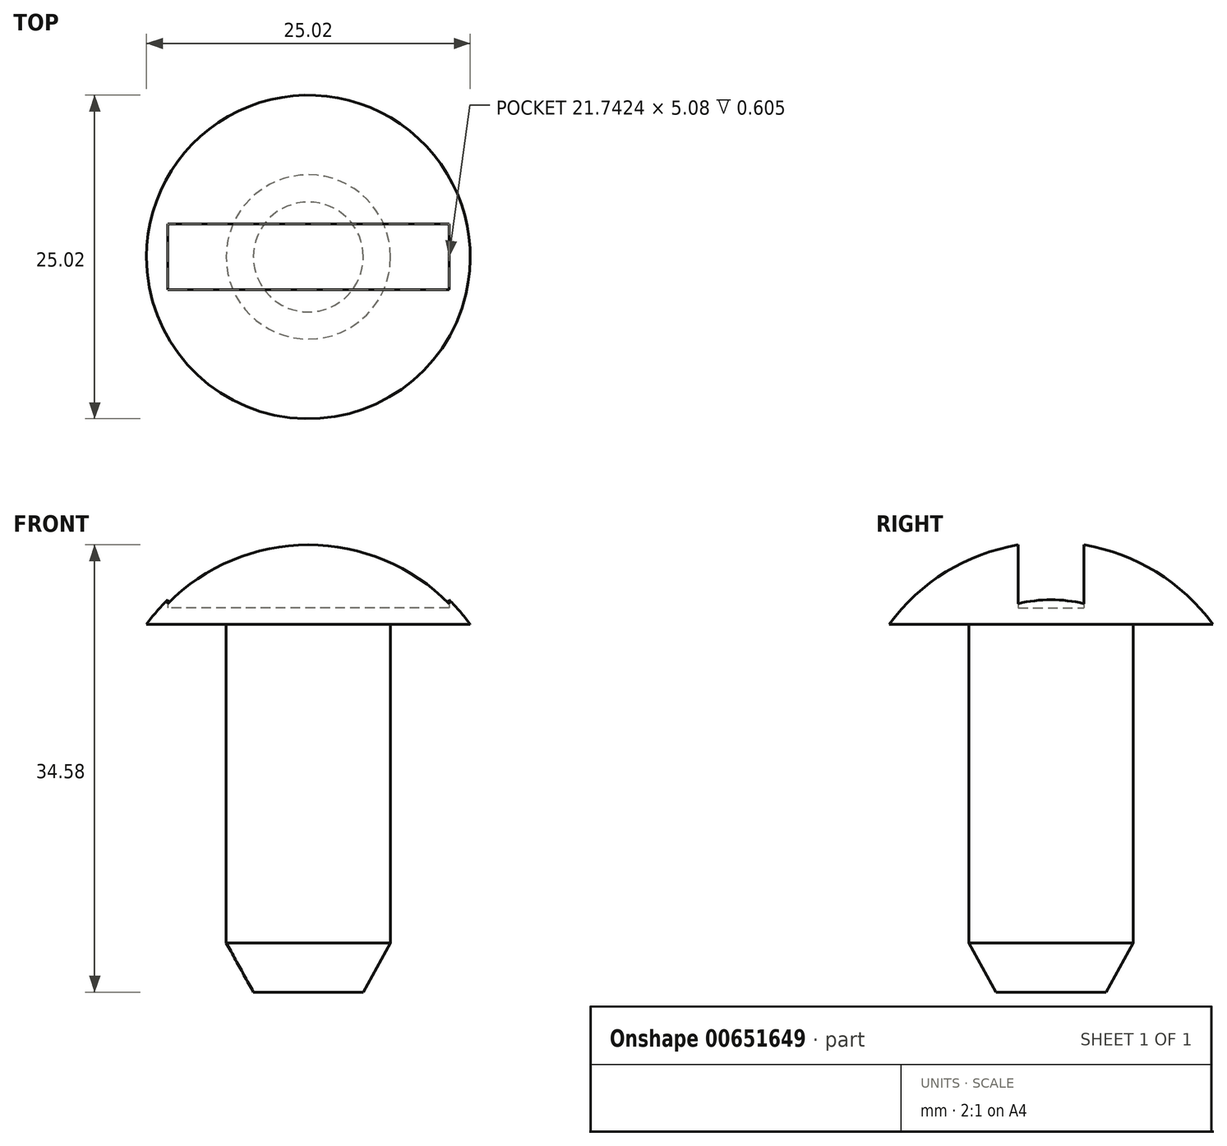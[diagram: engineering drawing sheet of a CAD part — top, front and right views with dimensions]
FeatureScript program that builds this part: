
annotation { "Feature Type Name" : "Feature", "Feature Type Description" : "" }
export const myFeature = defineFeature(function(context is Context, id is Id, definition is map)
    precondition{}
    {
        {
            var Q0;
            Q0=qCreatedBy(makeId("Front.planeOp"),FACE);
            var sketch = newSketch(context, id + "F0", { "sketchPlane" : qUnion([Q0])});
            skLineSegment(sketch, "E0", {"start": v(0, 0) * mm, "end": v(0, 30.98) * mm});
            skLineSegment(sketch, "E1", {"start": v(0, 0) * mm, "end": v(6.35, 0) * mm});
            skLineSegment(sketch, "E2", {"start": v(6.35, 0) * mm, "end": v(6.35, 24.63) * mm});
            skLineSegment(sketch, "E3", {"start": v(6.35, 24.63) * mm, "end": v(12.5, 24.63) * mm});
            skArc(sketch, "E4", {"start": v(12.5, 24.63) * mm, "mid": v(7.02, 29.3) * mm, "end": v(0, 30.98) * mm});
            skLineSegment(sketch, "E5", {"start": v(0, 0) * mm, "end": v(0, -3.8) * mm});
            skLineSegment(sketch, "E6", {"start": v(0, -3.8) * mm, "end": v(4.25, -3.8) * mm});
            skLineSegment(sketch, "E7", {"start": v(4.25, -3.81) * mm, "end": v(6.35, 0) * mm});
            skSolve(sketch);
        }
        {
            var Q0;
            Q0=makeQuery(id+"F0.imprint","IMPRINT",FACE,{"disambiguationData":[TD([[makeQuery(id+"F0.imprint","IMPRINT",EDGE,{"derivedFrom":sQuery(id+"F0.wireOp",EDGE,"E0")}),-1.0]])]});
            var Q1;
            Q1=makeQuery(id+"F0.imprint","IMPRINT",FACE,{"disambiguationData":[TD([[makeQuery(id+"F0.imprint","IMPRINT",EDGE,{"derivedFrom":sQuery(id+"F0.wireOp",EDGE,"E1")}),-1.0]])]});
            var Q2;
            Q2=sQuery(id+"F0.wireOp",EDGE,"E0");
            revolve(context, id + "F1", {"entities" : qUnion([Q0, Q1]), "axis" : qUnion([Q2]), "revolveType" : RevolveType.FULL});
        }
        {
            var Q0;
            Q0=qCreatedBy(makeId("Top.planeOp"),FACE);
            cPlane(context, id + "F2", {"entities" : qUnion([Q0]), "cplaneType" : CPlaneType.OFFSET, "offset" : 25.9 * mm, "width" : 152.4 * mm, "height" : 152.4 * mm});
        }
        {
            var Q0;
            Q0=qCreatedBy(id+"F2.planeOp",FACE);
            var sketch = newSketch(context, id + "F3", { "sketchPlane" : qUnion([Q0])});
            skLineSegment(sketch, "E8.bottom", {"start": v(10.87, -2.54) * mm, "end": v(-10.87, -2.54) * mm});
            skLineSegment(sketch, "E8.top", {"start": v(10.87, 2.54) * mm, "end": v(-10.87, 2.54) * mm});
            skLineSegment(sketch, "E8.left", {"start": v(10.87, -2.54) * mm, "end": v(10.87, 2.54) * mm});
            skLineSegment(sketch, "E8.right", {"start": v(-10.87, -2.54) * mm, "end": v(-10.87, 2.54) * mm});
            skPoint(sketch, "E8.middle", {"position": v(0, 0) * mm});
            skSolve(sketch);
        }
        {
            var Q0;
            Q0 = qSketchRegion(id + "F3", true);
            extrude(context, id + "F4", {"entities" : qUnion([Q0]), "operationType" : NewBodyOperationType.REMOVE, "endBound" : BoundingType.THROUGH_ALL, "depth" : 16.76 * mm, "offsetDistance" : 25.4 * mm});
        }
    });
